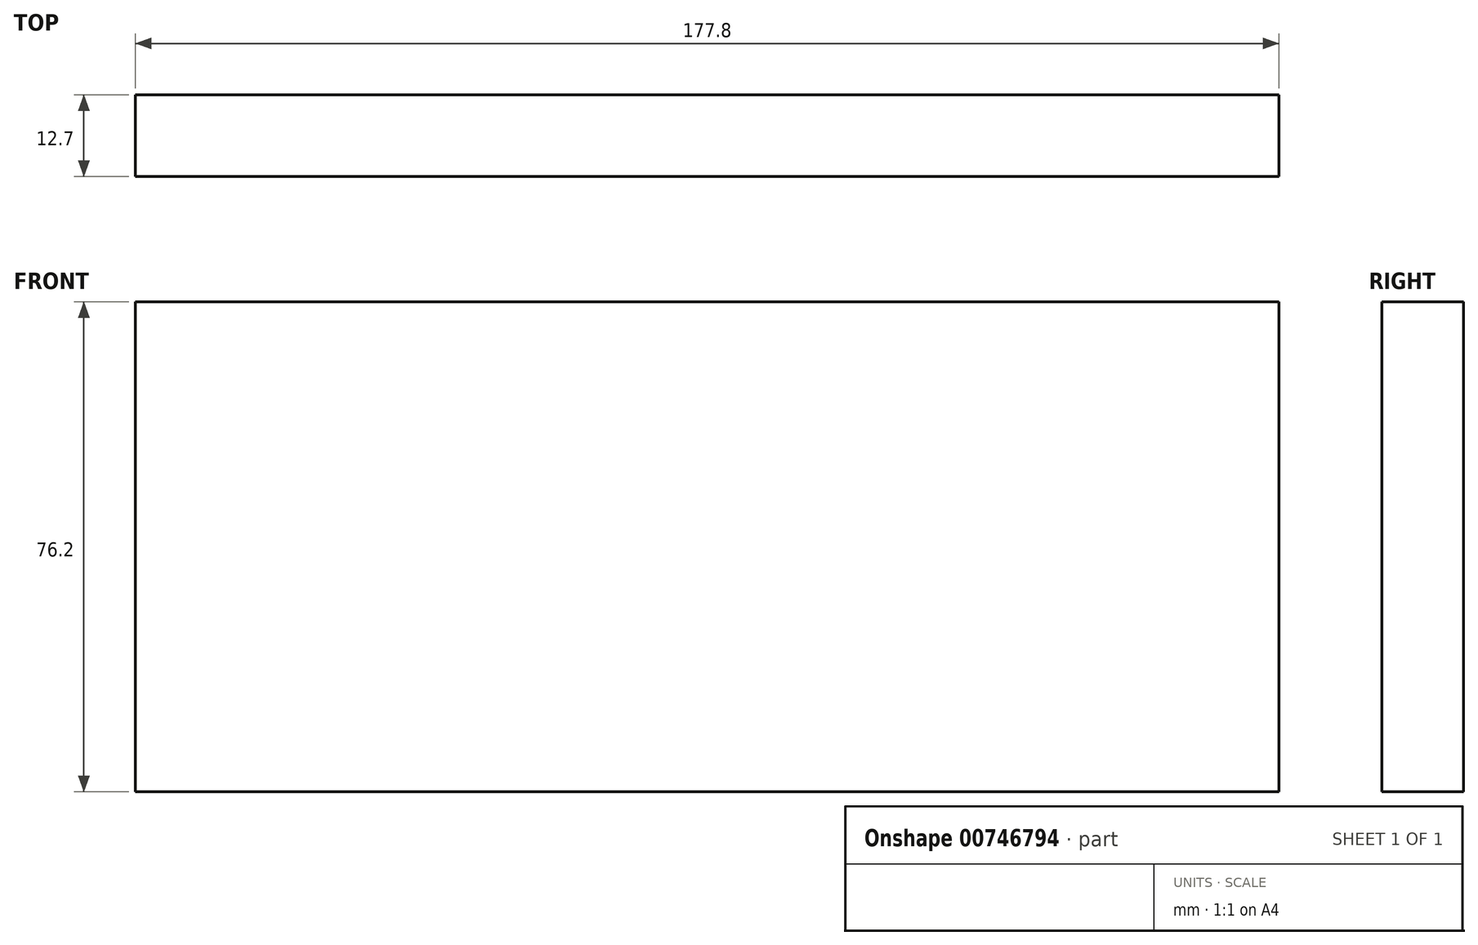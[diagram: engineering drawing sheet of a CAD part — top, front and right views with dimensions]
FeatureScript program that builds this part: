
annotation { "Feature Type Name" : "Feature", "Feature Type Description" : "" }
export const myFeature = defineFeature(function(context is Context, id is Id, definition is map)
    precondition{}
    {
        {
            var Q0;
            Q0=qCreatedBy(makeId("Front.planeOp"),FACE);
            var sketch = newSketch(context, id + "F0", { "sketchPlane" : qUnion([Q0])});
            skLineSegment(sketch, "E0.bottom", {"start": v(-38, 36.99) * mm, "end": v(139.8, 36.99) * mm});
            skLineSegment(sketch, "E0.top", {"start": v(-38, -39.21) * mm, "end": v(139.8, -39.21) * mm});
            skLineSegment(sketch, "E0.left", {"start": v(-38, 36.99) * mm, "end": v(-38, -39.21) * mm});
            skLineSegment(sketch, "E0.right", {"start": v(139.8, 36.99) * mm, "end": v(139.8, -39.21) * mm});
            skSolve(sketch);
        }
        {
            var Q0;
            Q0=makeQuery(id+"F0.imprint","IMPRINT",FACE,{"disambiguationData":[TD([[makeQuery(id+"F0.imprint","IMPRINT",EDGE,{"derivedFrom":sQuery(id+"F0.wireOp",EDGE,"E0.bottom")}),-1.0]])]});
            extrude(context, id + "F1", {"entities" : qUnion([Q0]), "depth" : 12.7 * mm, "offsetDistance" : 25.4 * mm});
        }
    });
